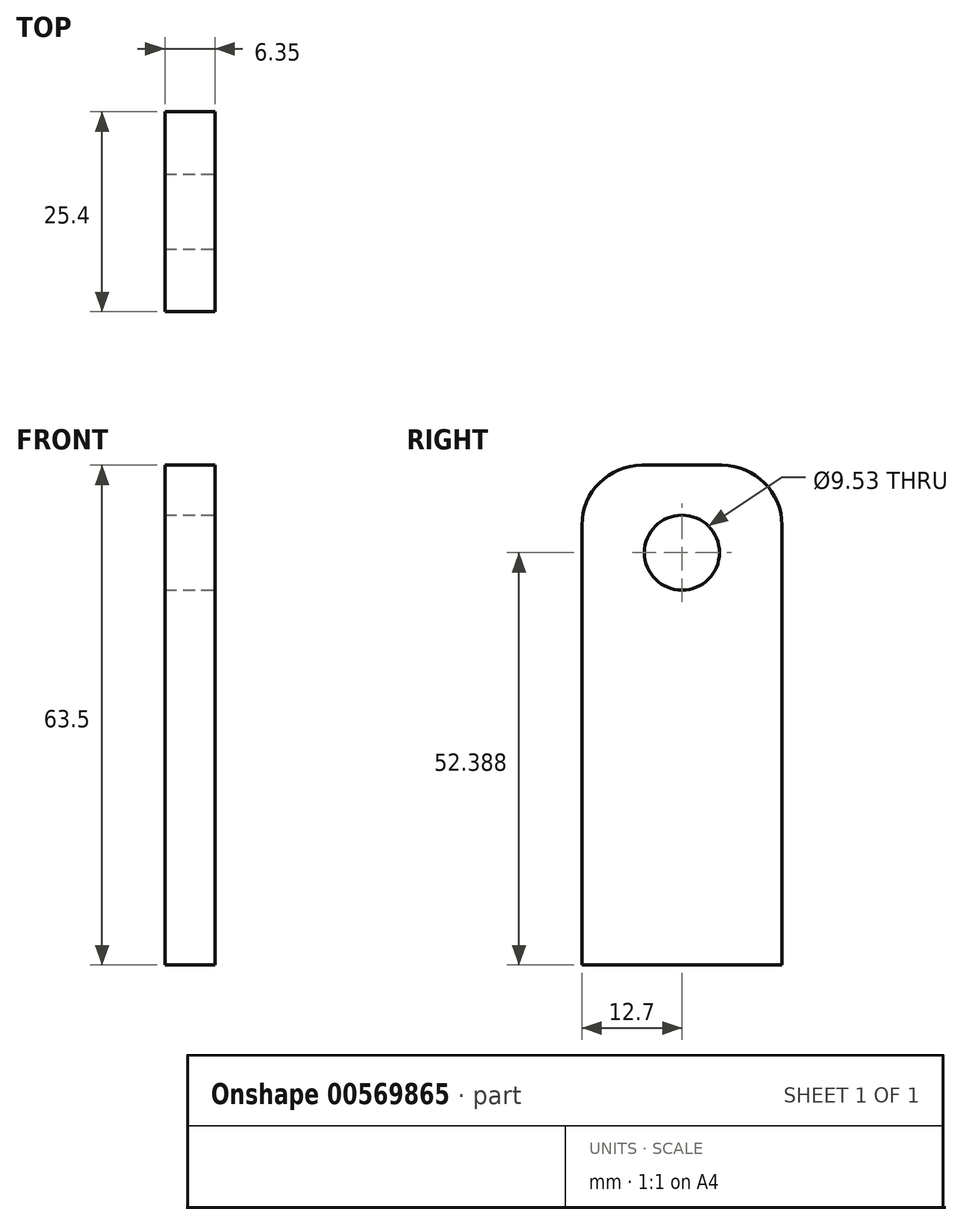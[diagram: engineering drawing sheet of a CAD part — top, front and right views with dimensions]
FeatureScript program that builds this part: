
annotation { "Feature Type Name" : "Feature", "Feature Type Description" : "" }
export const myFeature = defineFeature(function(context is Context, id is Id, definition is map)
    precondition{}
    {
        {
            var Q0;
            Q0=qCreatedBy(makeId("Front.planeOp"),FACE);
            var sketch = newSketch(context, id + "F0", { "sketchPlane" : qUnion([Q0])});
            skLineSegment(sketch, "E0.bottom", {"start": v(0, 0) * mm, "end": v(6.35, 0) * mm});
            skLineSegment(sketch, "E0.top", {"start": v(0, 63.5) * mm, "end": v(6.35, 63.5) * mm});
            skLineSegment(sketch, "E0.left", {"start": v(0, 0) * mm, "end": v(0, 63.5) * mm});
            skLineSegment(sketch, "E0.right", {"start": v(6.35, 0) * mm, "end": v(6.35, 63.5) * mm});
            skSolve(sketch);
        }
        {
            var Q0;
            Q0 = qSketchRegion(id + "F0", true);
            extrude(context, id + "F1", {"entities" : qUnion([Q0]), "depth" : 25.4 * mm, "offsetDistance" : 25.4 * mm});
        }
        {
            var Q0;
            Q0=makeQuery(id+"F1.opExtrude","CAP_EDGE",EDGE,{"disambiguationData":[OSD([sQuery(id+"F0.wireOp",EDGE,"E0.top")])],"isStart":false});
            var Q1;
            Q1=makeQuery(id+"F1.opExtrude","CAP_EDGE",EDGE,{"disambiguationData":[OSD([sQuery(id+"F0.wireOp",EDGE,"E0.top")])],"isStart":true});
            fillet(context, id + "F2", {"entities" : qUnion([Q0, Q1]), "radius" : 7.62 * mm, "tangentPropagation" : true, "allowEdgeOverflow" : false});
        }
        {
            var Q0;
            Q0=makeQuery(id+"F1.opExtrude","SWEPT_FACE",FACE,{"disambiguationData":[OSD([sQuery(id+"F0.wireOp",EDGE,"E0.right")])]});
            var sketch = newSketch(context, id + "F3", { "sketchPlane" : qUnion([Q0])});
            skCircle(sketch, "E1", {"center": v(-12.7, 52.39) * mm, "radius": 4.76 * mm});
            skSolve(sketch);
        }
        {
            var Q0;
            Q0=makeQuery(id+"F3.imprint","IMPRINT",FACE,{"disambiguationData":[TD([[makeQuery(id+"F3.imprint","IMPRINT",EDGE,{"derivedFrom":sQuery(id+"F3.wireOp",EDGE,"E1")}),1.0]])]});
            extrude(context, id + "F4", {"entities" : qUnion([Q0]), "operationType" : NewBodyOperationType.REMOVE, "oppositeDirection" : true, "depth" : 25.4 * mm, "offsetDistance" : 25.4 * mm});
        }
    });
